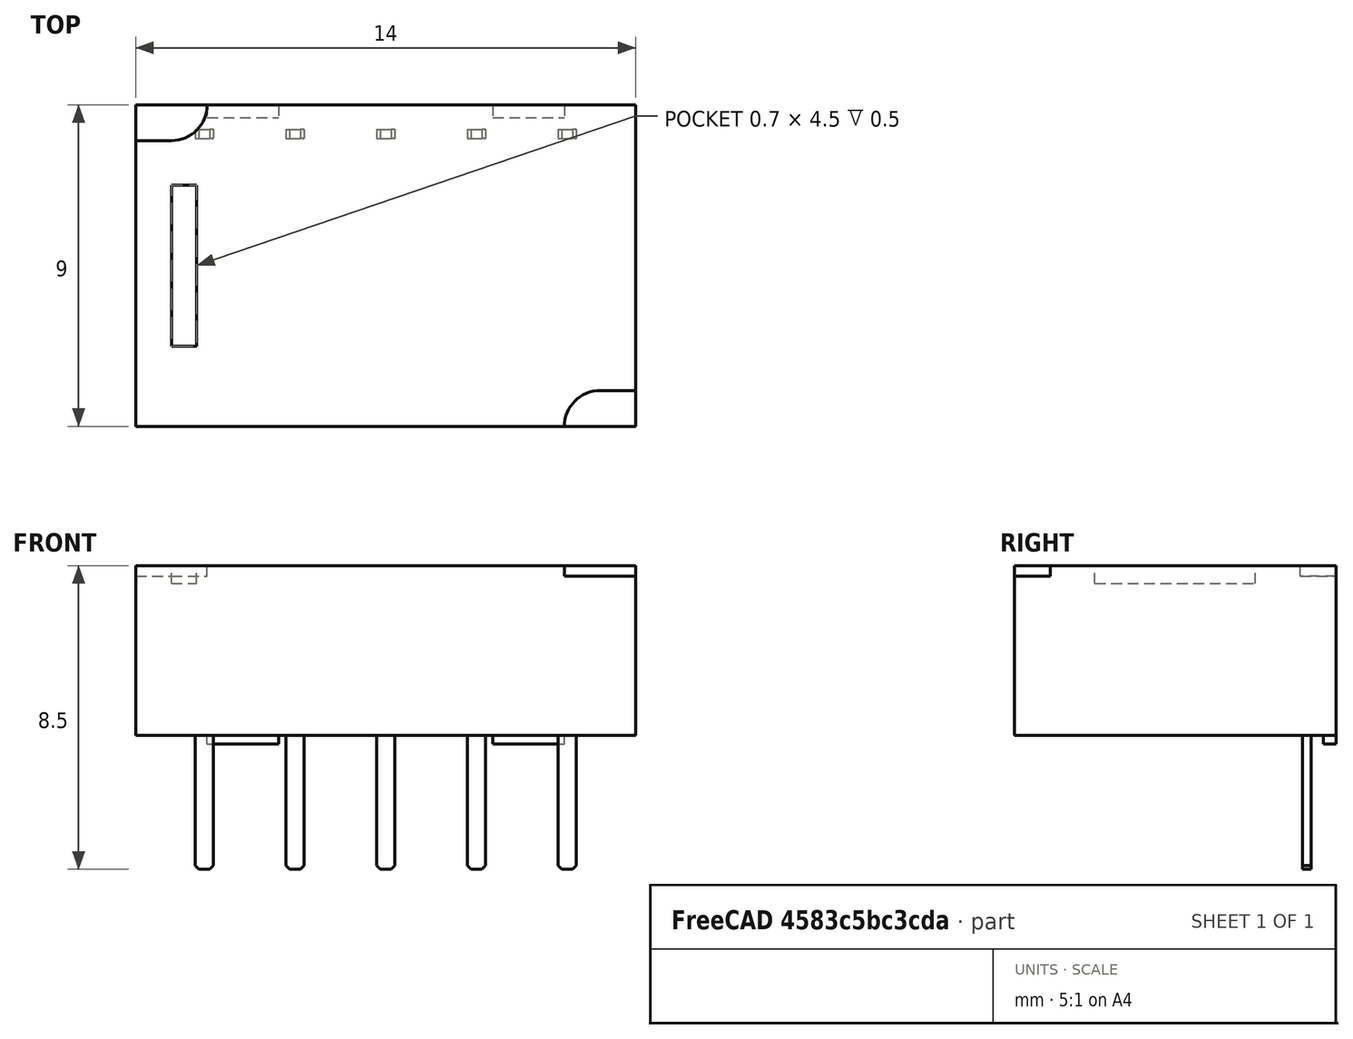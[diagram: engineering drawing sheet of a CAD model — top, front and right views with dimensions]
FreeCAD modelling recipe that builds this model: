
FCSTD DOCUMENT  (FreeCAD 0.18.4R)
Label: p5_ningbo
License: All rights reserved
LicenseURL: http://en.wikipedia.org/wiki/All_rights_reserved
objects: Part::Box×8, Part::Mirroring×7, Part::Cut×5, Part::Chamfer×5, Part::Cylinder×2
note: 27 computed .brp shape members not serialized (recipe doc carries the construction recipe); baked Part::Feature solids carry a one-line shape summary decoded from their .brp

FEATURE [Part::Box] Box  label="Cube"
  AttacherType = Attacher::AttachEngine3D
  Height = 4.75
  Length = 14
  Placement = pos=(-7,-4.5,0.25) rot=(0,0,1;0rad)
  Width = 9
FEATURE [Part::Box] Box001  label="Cube001"
  AttacherType = Attacher::AttachEngine3D
  Height = 0.5
  Length = 0.7
  Placement = pos=(-6,-2.25,4.5) rot=(0,0,1;0rad)
  Width = 4.5
FEATURE [Part::Box] Box002  label="Cube002"
  AttacherType = Attacher::AttachEngine3D
  Height = 0.5
  Length = 0.7
  Placement = pos=(-6,-2.25,4.5) rot=(0,0,1;0rad)
  Width = 4.5
FEATURE [Part::Cut] Cut
  Base = -> Box
  Tool = -> Box002
FEATURE [Part::Box] Box003  label="Cube003"
  AttacherType = Attacher::AttachEngine3D
  Height = 0.3
  Length = 1
  Placement = pos=(6,-4.5,4.7) rot=(0,0,1;0rad)
  Width = 1
FEATURE [Part::Box] Box004  label="Cube004"
  AttacherType = Attacher::AttachEngine3D
  Height = 0.3
  Length = 1
  Placement = pos=(-7,3.5,4.7) rot=(0,0,1;0rad)
  Width = 1
FEATURE [Part::Cylinder] Cylinder
  Angle = 360
  AttacherType = Attacher::AttachEngine3D
  Height = 0.3
  Placement = pos=(6,-4.5,4.7) rot=(0,0,1;0rad)
  Radius = 1
FEATURE [Part::Cylinder] Cylinder001
  Angle = 360
  AttacherType = Attacher::AttachEngine3D
  Height = 0.3
  Placement = pos=(-6,4.5,4.7) rot=(0,0,1;0rad)
  Radius = 1
FEATURE [Part::Cut] Cut001
  Base = -> Cut
  Tool = -> Box004
FEATURE [Part::Cut] Cut002
  Base = -> Cut001
  Tool = -> Cylinder001
FEATURE [Part::Cut] Cut003
  Base = -> Cut002
  Tool = -> Box003
FEATURE [Part::Cut] Cut004
  Base = -> Cut003
  Tool = -> Cylinder
FEATURE [Part::Box] Box005  label="sup2"
  AttacherType = Attacher::AttachEngine3D
  Height = 0.25
  Length = 2
  Placement = pos=(3,-4.5,0) rot=(0,0,1;0rad)
  Width = 0.35
FEATURE [Part::Box] Box006  label="Cube006"
  AttacherType = Attacher::AttachEngine3D
  Height = 3.75
  Length = 0.5
  Placement = pos=(-0.25,-3.81,-3.5) rot=(0,0,1;0rad)
  Width = 0.25
  expr: Placement.Base.y = -(7.62 / 2)
FEATURE [Part::Chamfer] Chamfer  label="pin3"
  Base = -> Box006
  Edges = 2 edges r=0.1: [Edge4,Edge8]
FEATURE [Part::Chamfer] Chamfer001  label="pin4"
  Base = -> Box006
  Edges = 2 edges r=0.1: [Edge4,Edge8]
  Placement = pos=(2.54,0,0) rot=(0,0,1;0rad)
FEATURE [Part::Chamfer] Chamfer002  label="pin5"
  Base = -> Box006
  Edges = 2 edges r=0.1: [Edge4,Edge8]
  Placement = pos=(5.08,0,0) rot=(0,0,1;0rad)
FEATURE [Part::Chamfer] Chamfer003  label="pin2"
  Base = -> Box006
  Edges = 2 edges r=0.1: [Edge4,Edge8]
  Placement = pos=(-2.54,0,0) rot=(0,0,1;0rad)
FEATURE [Part::Chamfer] Chamfer004  label="pin1"
  Base = -> Box006
  Edges = 2 edges r=0.1: [Edge4,Edge8]
  Placement = pos=(-5.08,0,0) rot=(0,0,1;0rad)
FEATURE [Part::Box] Box007  label="sup1"
  AttacherType = Attacher::AttachEngine3D
  Height = 0.25
  Length = 2
  Placement = pos=(-5,-4.5,0) rot=(0,0,1;0rad)
  Width = 0.35
FEATURE [Part::Mirroring] Part__Mirroring  label="pin3 (Mirror #1)"
  Base = (0,-2.38419e-07,-1.625)
  Normal = (0,1,-1.19209e-07)
  Source = -> Chamfer
FEATURE [Part::Mirroring] Part__Mirroring001  label="pin4 (Mirror #2)"
  Base = (2.54,-2.38419e-07,-1.625)
  Normal = (0,1,-1.19209e-07)
  Source = -> Chamfer001
FEATURE [Part::Mirroring] Part__Mirroring002  label="pin5 (Mirror #3)"
  Base = (5.08,-2.38419e-07,-1.625)
  Normal = (0,1,-1.19209e-07)
  Source = -> Chamfer002
FEATURE [Part::Mirroring] Part__Mirroring003  label="pin2 (Mirror #4)"
  Base = (0,0,0)
  Normal = (0,1,0)
  Source = -> Chamfer003
FEATURE [Part::Mirroring] Part__Mirroring004  label="pin1 (Mirror #5)"
  Base = (0,0,0)
  Normal = (0,1,0)
  Source = -> Chamfer004
FEATURE [Part::Mirroring] Part__Mirroring005  label="sup1 (Mirror #6)"
  Base = (0,0,0)
  Normal = (0,1,0)
  Source = -> Box007
FEATURE [Part::Mirroring] Part__Mirroring006  label="sup2 (Mirror #7)"
  Base = (0,0,0)
  Normal = (0,1,0)
  Source = -> Box005
